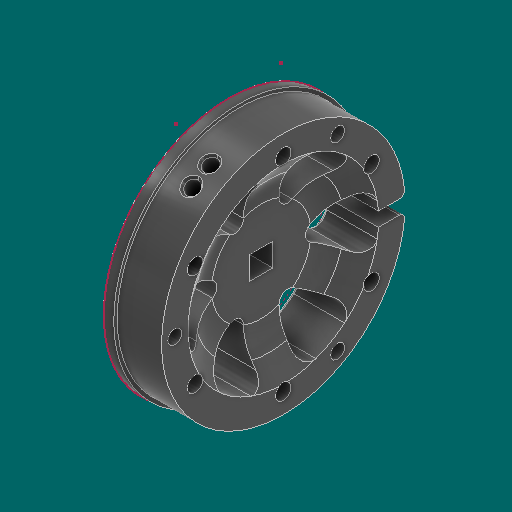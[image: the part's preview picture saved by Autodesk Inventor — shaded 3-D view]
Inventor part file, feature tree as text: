
AUTODESK INVENTOR PART (.ipt)
format: ipt  version: 2023.1 (Build 271208000, 208)  size: 551,936 bytes
history: native  units: in
note: dims shown in document units (in); Inventor stores cm internally (conversion verified against a paired STEP export)
features: sketch x5, other x3
ambient origin geometry x8: Origin, YZ Plane, XZ Plane, XY Plane, X Axis, Y Axis, Z Axis, Center Point
bodies: Solid1 (feature_tree)
feature tree (8):
  other  "WheelHalf.ipt"
  other  "Solid1::WheelHalf.ipt"
  other  "TaggingFeature1"
  sketch  "Sketch1"  dims[d0=0.3937in]
  sketch  "Sketch2"
  sketch  "Sketch3"
  sketch  "Sketch4"
  sketch  "Sketch5"
